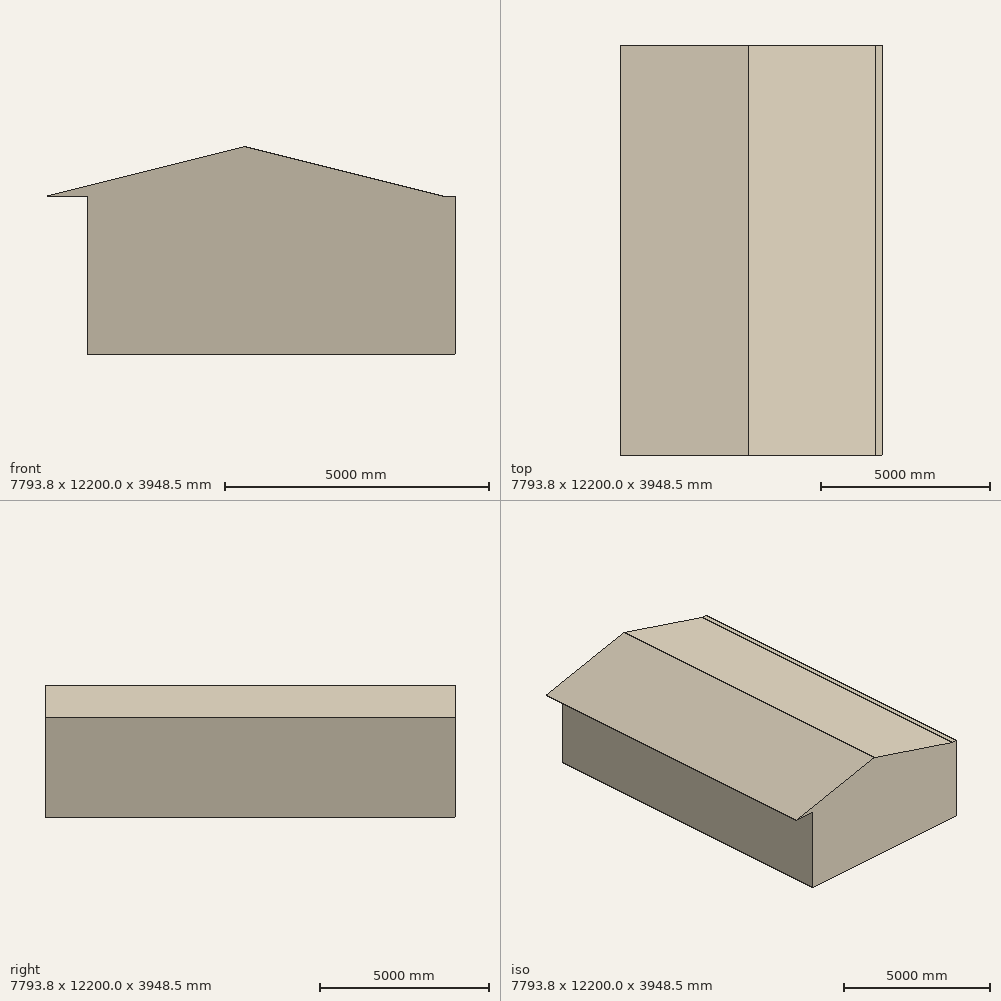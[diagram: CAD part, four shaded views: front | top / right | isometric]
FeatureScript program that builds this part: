
annotation { "Feature Type Name" : "Feature", "Feature Type Description" : "" }
export const myFeature = defineFeature(function(context is Context, id is Id, definition is map)
    precondition{}
    {
        {
            var Q0;
            Q0=qCreatedBy(makeId("Top.planeOp"),FACE);
            var sketch = newSketch(context, id + "F0", { "sketchPlane" : qUnion([Q0])});
            skLineSegment(sketch, "E0.bottom", {"start": v(0, 0) * mm, "end": v(7000, 0) * mm});
            skLineSegment(sketch, "E0.top", {"start": v(0, -12200) * mm, "end": v(7000, -12200) * mm});
            skLineSegment(sketch, "E0.left", {"start": v(0, 0) * mm, "end": v(0, -12200) * mm});
            skLineSegment(sketch, "E0.right", {"start": v(7000, 0) * mm, "end": v(7000, -12200) * mm});
            skSolve(sketch);
        }
        {
            var Q0;
            Q0 = qSketchRegion(id + "F0", true);
            extrude(context, id + "F1", {"entities" : qUnion([Q0]), "depth" : 3000 * mm, "offsetDistance" : 25 * mm});
        }
        {
            var Q0;
            Q0=makeQuery(id+"F1.opExtrude","SWEPT_FACE",FACE,{"disambiguationData":[OSD([sQuery(id+"F0.wireOp",EDGE,"E0.top")])]});
            var sketch = newSketch(context, id + "F2", { "sketchPlane" : qUnion([Q0])});
            skLineSegment(sketch, "E1", {"start": v(7000, 3000) * mm, "end": v(-1000, 3000) * mm});
            skLineSegment(sketch, "E2", {"start": v(-1000, 3000) * mm, "end": v(3000, 4000) * mm});
            skLineSegment(sketch, "E3", {"start": v(3000, 4000) * mm, "end": v(7000, 3000) * mm});
            skSolve(sketch);
        }
        {
            var Q0;
            Q0 = qSketchRegion(id + "F2", true);
            extrude(context, id + "F3", {"entities" : qUnion([Q0]), "operationType" : NewBodyOperationType.ADD, "oppositeDirection" : true, "depth" : 12200 * mm, "offsetDistance" : 25 * mm});
        }
        {
            var Q0;
            Q0=makeQuery(id+"F3.boolean.opBoolean","MERGE",FACE,{"derivedFrom":[makeQuery(id+"F1.opExtrude","SWEPT_FACE",FACE,{"disambiguationData":[OSD([sQuery(id+"F0.wireOp",EDGE,"E0.top")])]}),makeQuery(id+"F3.opExtrude","CAP_FACE",FACE,{"disambiguationData":[OSD([sQuery(id+"F2.wireOp",EDGE,"E1"),sQuery(id+"F2.wireOp",EDGE,"E2"),sQuery(id+"F2.wireOp",EDGE,"E3")])],"isStart":true})]});
            var sketch = newSketch(context, id + "F4", { "sketchPlane" : qUnion([Q0])});
            skLineSegment(sketch, "E4", {"start": v(-1000, 3000) * mm, "end": v(3000, 4000) * mm});
            skLineSegment(sketch, "E5", {"start": v(3000, 4000) * mm, "end": v(7000, 3000) * mm});
            skLineSegment(sketch, "E6", {"start": v(7000, 3000) * mm, "end": v(6793.84, 3000) * mm});
            skLineSegment(sketch, "E7", {"start": v(6793.84, 3000) * mm, "end": v(3000, 3948.46) * mm});
            skLineSegment(sketch, "E8", {"start": v(3000, 3948.46) * mm, "end": v(-793.84, 3000) * mm});
            skLineSegment(sketch, "E9", {"start": v(-793.84, 3000) * mm, "end": v(-1000, 3000) * mm});
            skSolve(sketch);
        }
        {
            var Q0;
            Q0 = qSketchRegion(id + "F4", true);
            extrude(context, id + "F5", {"entities" : qUnion([Q0]), "operationType" : NewBodyOperationType.REMOVE, "oppositeDirection" : true, "depth" : 18300 * mm, "offsetDistance" : 25 * mm});
        }
    });
